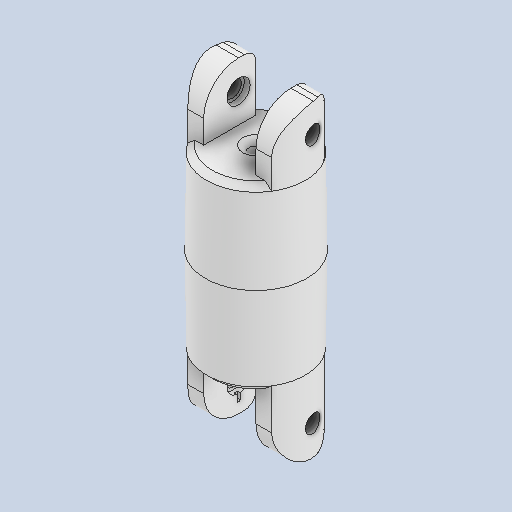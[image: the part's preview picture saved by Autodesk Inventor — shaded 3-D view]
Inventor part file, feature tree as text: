
AUTODESK INVENTOR PART (.ipt)
format: ipt  version: 2022 (Build 260153000, 153)  size: 316,416 bytes
history: native  units: in
note: dims shown in document units (in); Inventor stores cm internally (conversion verified against a paired STEP export)
features: sketch x14, extrude x10, fillet x6, hole x4, chamfer x4, thread x4
ambient origin geometry x8: Origin, YZ Plane, XZ Plane, XY Plane, X Axis, Y Axis, Z Axis, Center Point
bodies: Solid1 (feature_tree)
feature tree (42):
  extrude  "Extrusion1"  Depth=0.6693in
  extrude  "Extrusion2"  Depth=0.0394in TaperAngle=0.0deg
  fillet  "Fillet4"  Radius=0.2362in
  fillet  "Fillet5"  Radius=0.0787in
  hole  "Hole2"  [1 undecoded]
  hole  "Hole3"  [1 undecoded]
  extrude  "Extrusion5"  Depth=0.0197in TaperAngle=0.0deg
  extrude  "Extrusion6"  Depth=0.0394in TaperAngle=45.0deg
  extrude  "Extrusion7"  Depth=0.685in
  extrude  "Extrusion8"  Depth=0.5709in TaperAngle=45.0deg
  chamfer  "Chamfer3"  Distance=0.685in
  fillet  "Fillet6"  Radius=0.0394in
  extrude  "Extrusion9"  Depth=0.3937in TaperAngle=0.0deg
  chamfer  "Chamfer4"  Distance=0.1969in
  chamfer  "Chamfer5"  Distance=0.0394in Angle=45.0deg
  extrude  "Extrusion11"  Depth=0.2362in TaperAngle=0.0deg
  fillet  "Fillet7"  Radius=0.2362in
  fillet  "Fillet8"  Radius=0.2362in
  fillet  "Fillet9"  Radius=0.2362in
  hole  "Hole4"  [1 undecoded]
  hole  "Hole5"  [1 undecoded]
  chamfer  "Chamfer6"  Distance=0.0197in
  thread  "Thread1"  [1 undecoded]
  thread  "Thread2"  [1 undecoded]
  thread  "Thread3"  [1 undecoded]
  thread  "Thread4"  [1 undecoded]
  sketch  "Sketch1"  dims[d9=0.4724in d10=0.0in d11=0.6693in]
  sketch  "Sketch2"  dims[d12=0.0984in d13=0.0394in d14=0.0in d28=0.2362in d29=0.0787in]
  sketch  "Sketch4"  dims[d30=0.1969in]
  sketch  "Sketch5"  dims[d31=0.1181in d32=0.2362in d33=0.1575in d34=0.0394in d35=90.0deg d36=0.1575in d37=0.0in d38=0.1969in]
  sketch  "Sketch8"  dims[d39=0.1181in d40=0.2362in d41=0.1575in d42=0.0394in d43=90.0deg d44=0.1575in d45=0.0in d61=0.0197in d62=0.0in]
  sketch  "Sketch9"  dims[d63=0.0197in d64=0.0in d68=0.0197in d69=0.0in]
  sketch  "Sketch10"  dims[d70=0.0197in d71=0.0in d72=0.0394in d73=0.0492in d74=45.0deg]
  sketch  "Sketch11"  dims[d75=0.0394in d76=0.685in]
  sketch  "Sketch12"  dims[d77=0.5709in d78=0.0in d79=0.5709in d80=0.0079in d81=45.0deg d82=0.685in d84=0.0in d85=0.5709in]
  sketch  "Sketch14"  dims[d91=0.0394in d93=0.0in d94=0.3937in]
  sketch  "Sketch16"  dims[d96=0.0787in]
  sketch  "Sketch17"  dims[d97=0.1969in d98=0.1181in d99=0.2362in d100=0.1575in d101=0.0394in d102=90.0deg d103=0.1575in d104=0.0in d105=0.1969in d106=0.1181in d107=0.2362in d108=0.1575in d109=0.0394in d110=90.0deg d111=0.1575in d112=0.0in d113=0.0394in d114=0.0787in d115=45.0deg d116=0.2362in d117=0.0in d118=0.2362in d119=0.0in d120=0.2362in d121=0.0in d122=0.2362in d123=0.0in d50=0.0197in d51=0.0344in d52=0.0197in d53=0.0344in]
  sketch  "Sketch13"  dims[d86=0.0079in d87=0.5709in d88=45.0deg d89=0.0394in d90=0.0in]
  sketch  "Sketch15"  dims[d95=0.2362in]
  extrude  "Extrusion10"  [1 undecoded]
  extrude  "Extrusion12"  [1 undecoded]
note: 10 required parameter values undecoded (feature->parameter linkage not recoverable at this tier; creation-order binding heuristic only, values carry confidence <= 0.55)
